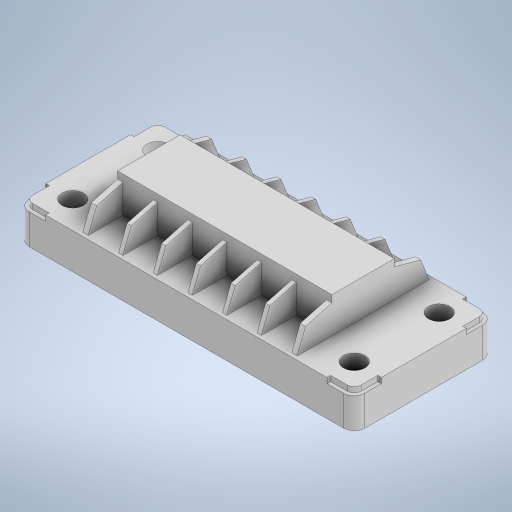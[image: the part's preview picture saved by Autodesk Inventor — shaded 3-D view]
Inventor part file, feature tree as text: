
AUTODESK INVENTOR PART (.ipt)
format: ipt  version: 2024 (Build 280153000, 153)  size: 443,904 bytes
history: native  units: in
note: dims shown in document units (in); Inventor stores cm internally (conversion verified against a paired STEP export)
features: sketch x6, extrude x5, mirror x3, pattern_linear x1, hole x1, fillet x1
ambient origin geometry x8: Origin, YZ Plane, XZ Plane, XY Plane, X Axis, Y Axis, Z Axis, Center Point
bodies: Solid1 (feature_tree)
feature tree (17):
  extrude  "Extrusion1"  Depth=4.7in
  extrude  "Extrusion2"  Depth=1.95in
  extrude  "Extrusion3"  Depth=0.85in
  pattern_linear  "Rectangular Pattern1"  Spacing1=0.85in  [1 undecoded]
  extrude  "Extrusion4"  Depth=0.5in TaperAngle=0.0deg
  mirror  "Mirror1"
  hole  "Hole1"  [1 undecoded]
  mirror  "Mirror2"
  fillet  "Fillet1"  Radius=0.425in
  extrude  "Extrusion5"  Depth=0.1in
  mirror  "Mirror3"
  sketch  "Sketch1"  dims[d0=4.7in d1=2.35in]
  sketch  "Sketch2"  dims[d2=1.95in d3=0.975in]
  sketch  "Sketch3"  dims[d4=0.5in d5=0.0in d6=0.85in]
  sketch  "Sketch4"  dims[d7=3.0in]
  sketch  "Sketch5"  dims[d8=0.05in]
  sketch  "Sketch6"  dims[d9=1.85in d10=0.85in d11=0.5in d12=0.0in d13=0.075in d14=0.425in d15=0.4375in d16=0.5in d17=0.0in d18=2.3622in d20=0.485in d21=0.7874in d23=-1.3625in d24=0.05in d25=0.05in d26=0.33in d27=0.05in d28=0.05in d29=0.075in d30=0.0in d31=0.3in d32=0.75in d33=0.375in d34=0.25in d35=0.5635in d36=1.0in d37=0.8108in d38=0.38in d39=0.38in d40=0.38in d41=0.38in d42=0.15in d43=0.1in d44=0.3in d45=0.4875in d46=0.1in d47=0.1in d49=0.12in d50=0.0in d51=0.0in]
note: 2 required parameter values undecoded (feature->parameter linkage not recoverable at this tier; creation-order binding heuristic only, values carry confidence <= 0.55)
